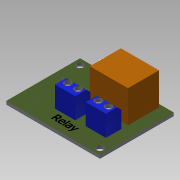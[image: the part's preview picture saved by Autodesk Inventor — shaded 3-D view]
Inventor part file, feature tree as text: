
AUTODESK INVENTOR PART (.ipt)
format: ipt  version: 2015 SP1 (Build 190203100, 203)  size: 381,440 bytes
history: native  units: mm
features: extrude x6, sketch x3, chamfer x1
ambient origin geometry x8: Origin, YZ Plane, XZ Plane, XY Plane, X Axis, Y Axis, Z Axis, Center Point
bodies: Solid1 (feature_tree)
feature tree (10):
  sketch  "Sketch1"  dims[d0=46.25mm d1=36.41mm]
  extrude  "Extrusion1"  Depth=36.41mm
  extrude  "Extrusion2"  Depth=3.0mm
  extrude  "Extrusion3"  Depth=3.0mm
  extrude  "Extrusion4"  Depth=3.0mm
  chamfer  "Chamfer1"  Distance=18.79mm
  extrude  "Extrusion5"  Depth=15.32mm
  sketch  "Sketch2"  dims[d5=3.0mm d6=3.0mm]
  extrude  "Extrusion6"  Depth=24.243896mm
  sketch  "Sketch3"  dims[d7=3.5mm d8=3.0mm d9=3.0mm d10=18.79mm d11=15.32mm d12=24.243896mm d13=24.243896mm d14=5.81mm d15=1.5mm d16=1.0mm d17=8.76mm d18=6.0mm d19=1.0mm d20=1.0mm d21=2.54mm d22=2.54mm d23=5.0mm d25=3.5mm d26=3.5mm d28=5.0mm d29=10.0mm d30=7.5mm d31=3.5mm d32=3.5mm d33=5.0mm d34=2.5mm d35=10.0mm d36=7.5mm d37=1.6mm d38=0.0mm d39=17.44mm d40=0.0mm d41=10.15mm d42=0.0mm d43=11.88mm d44=0.0mm d45=2.0mm d46=2.0mm d47=45.0deg d48=10.0mm d49=0.0mm d50=10.0mm d51=0.0mm]
